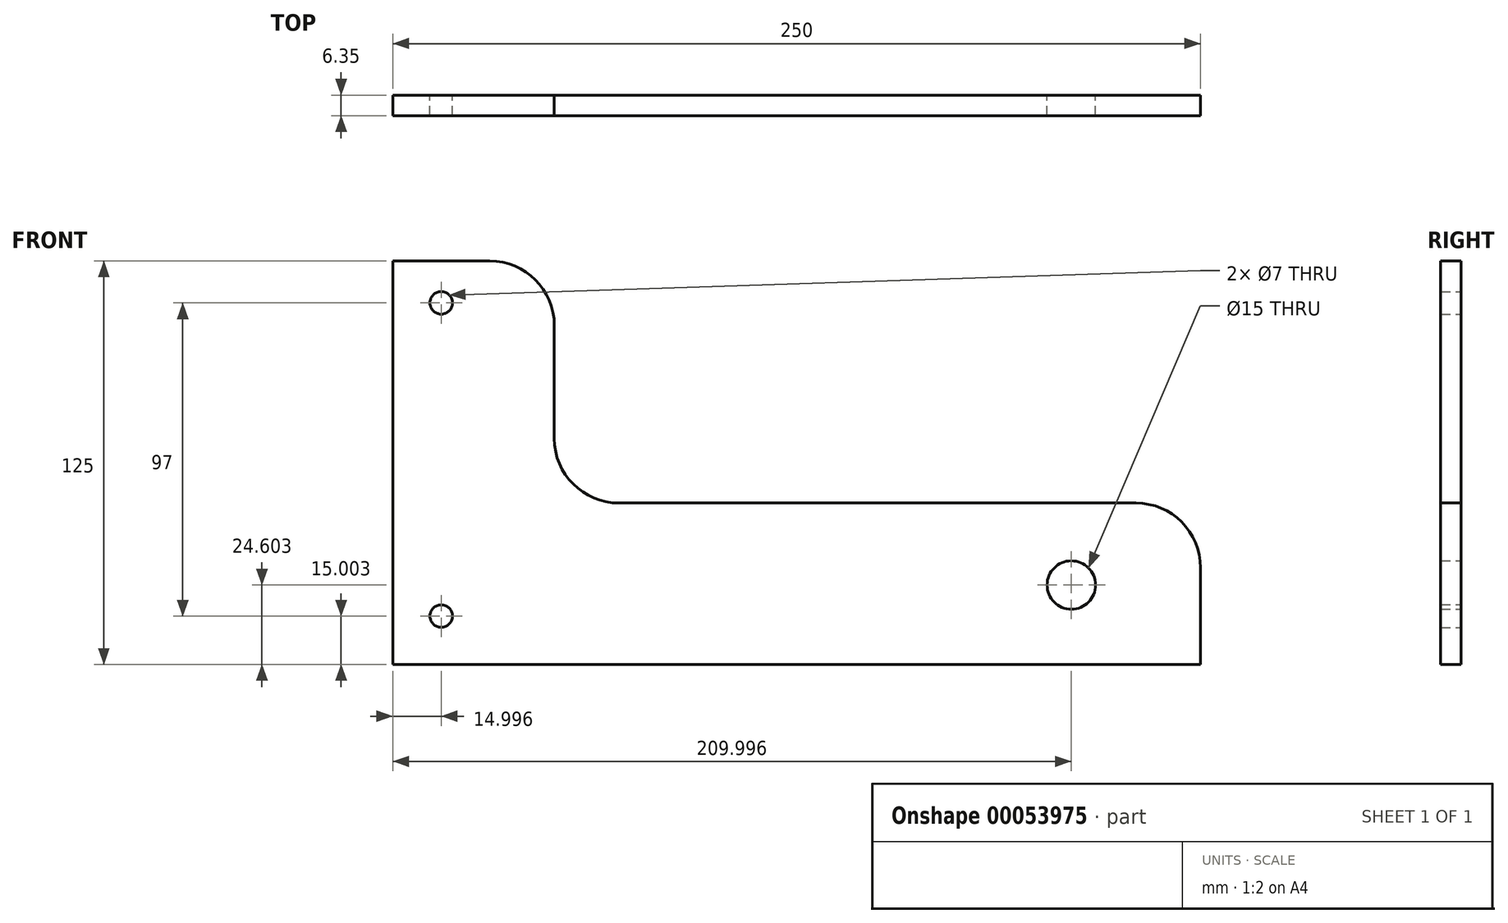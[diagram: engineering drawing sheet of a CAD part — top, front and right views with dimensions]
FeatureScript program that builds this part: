
annotation { "Feature Type Name" : "Feature", "Feature Type Description" : "" }
export const myFeature = defineFeature(function(context is Context, id is Id, definition is map)
    precondition{}
    {
        {
            var Q0;
            Q0=qCreatedBy(makeId("Front.planeOp"),FACE);
            var sketch = newSketch(context, id + "F0", { "sketchPlane" : qUnion([Q0])});
            skLineSegment(sketch, "E0", {"start": v(-109.3, 62.53) * mm, "end": v(-109.3, -62.47) * mm});
            skLineSegment(sketch, "E1", {"start": v(-109.3, -62.47) * mm, "end": v(140.7, -62.47) * mm});
            skLineSegment(sketch, "E2", {"start": v(140.7, -62.47) * mm, "end": v(140.7, -32.47) * mm});
            skLineSegment(sketch, "E3", {"start": v(120.7, -12.47) * mm, "end": v(-39.3, -12.47) * mm});
            skLineSegment(sketch, "E4", {"start": v(-59.3, 7.53) * mm, "end": v(-59.3, 42.53) * mm});
            skLineSegment(sketch, "E5", {"start": v(-79.3, 62.53) * mm, "end": v(-109.3, 62.53) * mm});
            skPoint(sketch, "E6.visualSharp", {"position": v(-59.3, 62.53) * mm});
            skArc(sketch, "E6.filletArc", {"start": v(-59.3, 42.53) * mm, "mid": v(-65.15, 56.68) * mm, "end": v(-79.3, 62.53) * mm});
            skPoint(sketch, "E7.visualSharp", {"position": v(-59.3, -12.47) * mm});
            skArc(sketch, "E7.filletArc", {"start": v(-59.3, 7.53) * mm, "mid": v(-53.44, -6.6) * mm, "end": v(-39.3, -12.47) * mm});
            skPoint(sketch, "E8.visualSharp", {"position": v(140.7, -12.47) * mm});
            skArc(sketch, "E8.filletArc", {"start": v(140.7, -32.47) * mm, "mid": v(134.85, -18.32) * mm, "end": v(120.7, -12.47) * mm});
            skSolve(sketch);
        }
        {
            var Q0;
            Q0 = qSketchRegion(id + "F0", true);
            extrude(context, id + "F1", {"entities" : qUnion([Q0]), "depth" : 6.35 * mm});
        }
        {
            var Q0;
            Q0=qCreatedBy(makeId("Front.planeOp"),FACE);
            var sketch = newSketch(context, id + "F2", { "sketchPlane" : qUnion([Q0])});
            skPoint(sketch, "E9", {"position": v(-94.3, 49.53) * mm});
            skPoint(sketch, "E10", {"position": v(-94.3, -47.47) * mm});
            skPoint(sketch, "E11", {"position": v(100.7, -37.87) * mm});
            skSolve(sketch);
        }
        {
            var Q0;
            Q0=sQuery(id+"F2.wireOp",VERTEX,"E9");
            var Q1;
            Q1=sQuery(id+"F2.wireOp",VERTEX,"E10");
            var Q2;
            Q2=makeQuery(id+"F1.opExtrude","SWEPT_BODY",BODY,{"disambiguationData":[OSD([sQuery(id+"F0.wireOp",EDGE,"E0"),sQuery(id+"F0.wireOp",EDGE,"E1"),sQuery(id+"F0.wireOp",EDGE,"E2"),sQuery(id+"F0.wireOp",EDGE,"E3"),sQuery(id+"F0.wireOp",EDGE,"E4"),sQuery(id+"F0.wireOp",EDGE,"E5"),sQuery(id+"F0.wireOp",EDGE,"E6.filletArc"),sQuery(id+"F0.wireOp",EDGE,"E7.filletArc"),sQuery(id+"F0.wireOp",EDGE,"E8.filletArc")])]});
            hole(context, id + "F3", {"style" : HoleStyle.SIMPLE, "holeDiameter" : 7 * mm, "endStyle" : HoleEndStyle.THROUGH, "oppositeDirection" : true, "locations" : qUnion([Q0, Q1]), "scope" : qUnion([Q2])});
        }
        {
            var Q0;
            Q0=sQuery(id+"F2.wireOp",VERTEX,"E11");
            var Q1;
            Q1=makeQuery(id+"F1.opExtrude","SWEPT_BODY",BODY,{"disambiguationData":[OSD([sQuery(id+"F0.wireOp",EDGE,"E0"),sQuery(id+"F0.wireOp",EDGE,"E1"),sQuery(id+"F0.wireOp",EDGE,"E2"),sQuery(id+"F0.wireOp",EDGE,"E3"),sQuery(id+"F0.wireOp",EDGE,"E4"),sQuery(id+"F0.wireOp",EDGE,"E5"),sQuery(id+"F0.wireOp",EDGE,"E6.filletArc"),sQuery(id+"F0.wireOp",EDGE,"E7.filletArc"),sQuery(id+"F0.wireOp",EDGE,"E8.filletArc")])]});
            hole(context, id + "F4", {"style" : HoleStyle.SIMPLE, "holeDiameter" : 15 * mm, "endStyle" : HoleEndStyle.THROUGH, "oppositeDirection" : true, "locations" : qUnion([Q0]), "scope" : qUnion([Q1])});
        }
    });
